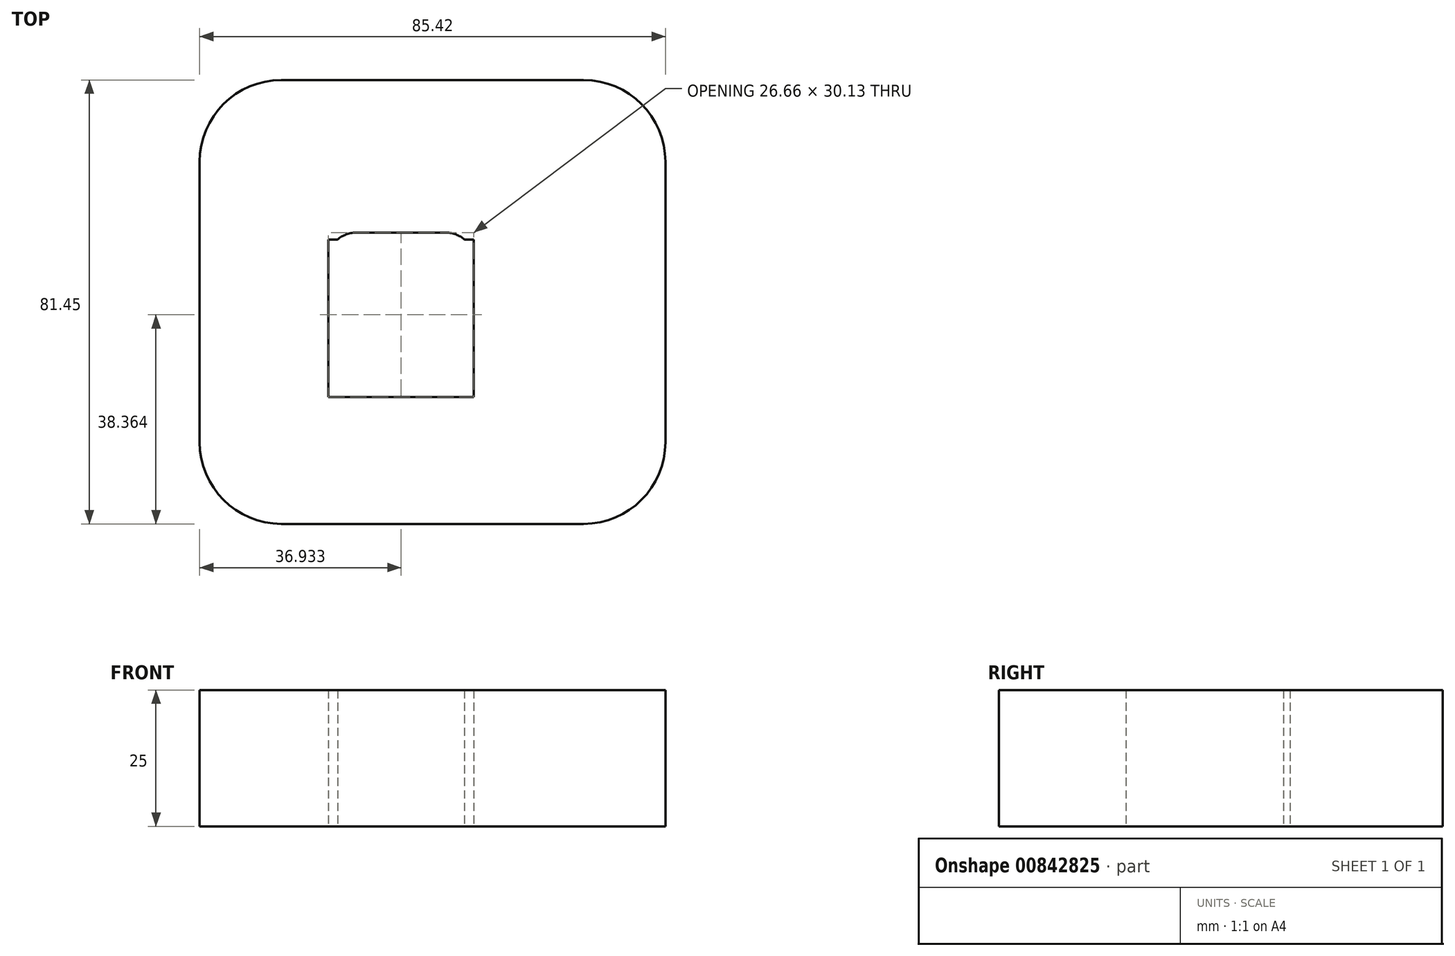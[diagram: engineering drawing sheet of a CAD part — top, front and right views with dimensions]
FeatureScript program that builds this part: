
annotation { "Feature Type Name" : "Feature", "Feature Type Description" : "" }
export const myFeature = defineFeature(function(context is Context, id is Id, definition is map)
    precondition{}
    {
        {
            var Q0;
            Q0=qCreatedBy(makeId("Top.planeOp"),FACE);
            var sketch = newSketch(context, id + "F0", { "sketchPlane" : qUnion([Q0])});
            skLineSegment(sketch, "E0", {"start": v(-27.71, 47.59) * mm, "end": v(27.71, 47.59) * mm});
            skLineSegment(sketch, "E1", {"start": v(42.71, 32.59) * mm, "end": v(42.71, -18.86) * mm});
            skLineSegment(sketch, "E2", {"start": v(27.71, -33.86) * mm, "end": v(-27.71, -33.86) * mm});
            skLineSegment(sketch, "E3", {"start": v(-42.71, -18.86) * mm, "end": v(-42.71, 32.59) * mm});
            skLineSegment(sketch, "E4", {"start": v(-42.71, 37.59) * mm, "end": v(-39.3, 37.59) * mm});
            skPoint(sketch, "E5.newPointA", {"position": v(-42.71, 47.59) * mm});
            skPoint(sketch, "E5.newPointB", {"position": v(-29.3, 47.59) * mm});
            skArc(sketch, "E5.filletArc", {"start": v(-27.71, 47.59) * mm, "mid": v(-38.32, 43.2) * mm, "end": v(-42.71, 32.59) * mm});
            skPoint(sketch, "E6.visualSharp", {"position": v(42.71, 47.59) * mm});
            skArc(sketch, "E6.filletArc", {"start": v(42.71, 32.59) * mm, "mid": v(38.32, 43.2) * mm, "end": v(27.71, 47.59) * mm});
            skPoint(sketch, "E7.visualSharp", {"position": v(42.71, -33.86) * mm});
            skArc(sketch, "E7.filletArc", {"start": v(27.71, -33.86) * mm, "mid": v(38.32, -29.47) * mm, "end": v(42.71, -18.86) * mm});
            skPoint(sketch, "E8.visualSharp", {"position": v(-42.71, -33.86) * mm});
            skArc(sketch, "E8.filletArc", {"start": v(-42.71, -18.86) * mm, "mid": v(-38.32, -29.47) * mm, "end": v(-27.71, -33.86) * mm});
            skLineSegment(sketch, "E9.bottom", {"start": v(-19.1, -10.56) * mm, "end": v(7.55, -10.56) * mm});
            skLineSegment(sketch, "E9.top", {"start": v(-14.1, -10.56) * mm, "end": v(2.55, -10.56) * mm});
            skLineSegment(sketch, "E9.left", {"start": v(-19.1, -10.56) * mm, "end": v(-19.1, -10.56) * mm});
            skLineSegment(sketch, "E9.right", {"start": v(7.55, -10.56) * mm, "end": v(7.55, -10.56) * mm});
            skLineSegment(sketch, "E10.top", {"start": v(7.55, 18.33) * mm, "end": v(7.55, 18.33) * mm});
            skLineSegment(sketch, "E10.left", {"start": v(7.55, -10.56) * mm, "end": v(7.55, 18.33) * mm});
            skLineSegment(sketch, "E10.right", {"start": v(7.55, -5.56) * mm, "end": v(7.55, 14.57) * mm});
            skLineSegment(sketch, "E11.top", {"start": v(-19.1, 19.57) * mm, "end": v(-19.1, 19.57) * mm});
            skLineSegment(sketch, "E11.left", {"start": v(-19.1, -10.56) * mm, "end": v(-19.1, 19.57) * mm});
            skLineSegment(sketch, "E11.right", {"start": v(-19.1, -5.56) * mm, "end": v(-19.1, 14.57) * mm});
            skLineSegment(sketch, "E12.bottom", {"start": v(-14.1, 19.57) * mm, "end": v(2.55, 19.57) * mm});
            skLineSegment(sketch, "E12.top", {"start": v(-19.1, 18.33) * mm, "end": v(7.55, 18.33) * mm});
            skLineSegment(sketch, "E12.left", {"start": v(-19.1, 19.57) * mm, "end": v(-19.1, 18.33) * mm});
            skLineSegment(sketch, "E12.right", {"start": v(7.55, 19.57) * mm, "end": v(7.55, 18.33) * mm});
            skPoint(sketch, "E13.visualSharp", {"position": v(7.55, -10.56) * mm});
            skArc(sketch, "E13.filletArc", {"start": v(2.55, -10.56) * mm, "mid": v(6.09, -9.1) * mm, "end": v(7.55, -5.56) * mm});
            skPoint(sketch, "E14.visualSharp", {"position": v(-19.1, -10.56) * mm});
            skArc(sketch, "E14.filletArc", {"start": v(-19.1, -5.56) * mm, "mid": v(-17.64, -9.1) * mm, "end": v(-14.1, -10.56) * mm});
            skPoint(sketch, "E15.visualSharp", {"position": v(-19.1, 19.57) * mm});
            skArc(sketch, "E15.filletArc", {"start": v(-14.1, 19.57) * mm, "mid": v(-17.64, 18.1) * mm, "end": v(-19.1, 14.57) * mm});
            skArc(sketch, "E16.filletArc", {"start": v(7.55, 14.57) * mm, "mid": v(6.09, 18.1) * mm, "end": v(2.55, 19.57) * mm});
            skLineSegment(sketch, "E17", {"start": v(-19.1, -5.56) * mm, "end": v(-42.71, -18.86) * mm});
            skLineSegment(sketch, "E18", {"start": v(-14.1, -10.56) * mm, "end": v(-27.71, -33.86) * mm});
            skLineSegment(sketch, "E19", {"start": v(2.55, -10.56) * mm, "end": v(27.71, -33.86) * mm});
            skLineSegment(sketch, "E20", {"start": v(7.55, -5.56) * mm, "end": v(42.71, -18.86) * mm});
            skLineSegment(sketch, "E21", {"start": v(7.55, 14.57) * mm, "end": v(42.71, 32.59) * mm});
            skLineSegment(sketch, "E22", {"start": v(2.55, 19.57) * mm, "end": v(27.71, 47.59) * mm});
            skLineSegment(sketch, "E23", {"start": v(-14.1, 19.57) * mm, "end": v(-27.71, 47.59) * mm});
            skLineSegment(sketch, "E24", {"start": v(-19.1, 14.57) * mm, "end": v(-42.71, 32.59) * mm});
            skSolve(sketch);
        }
        {
            var Q0;
            Q0 = qSketchRegion(id + "F0", true);
            extrude(context, id + "F1", {"entities" : qUnion([Q0]), "depth" : 25 * mm, "offsetDistance" : 25 * mm});
        }
    });
